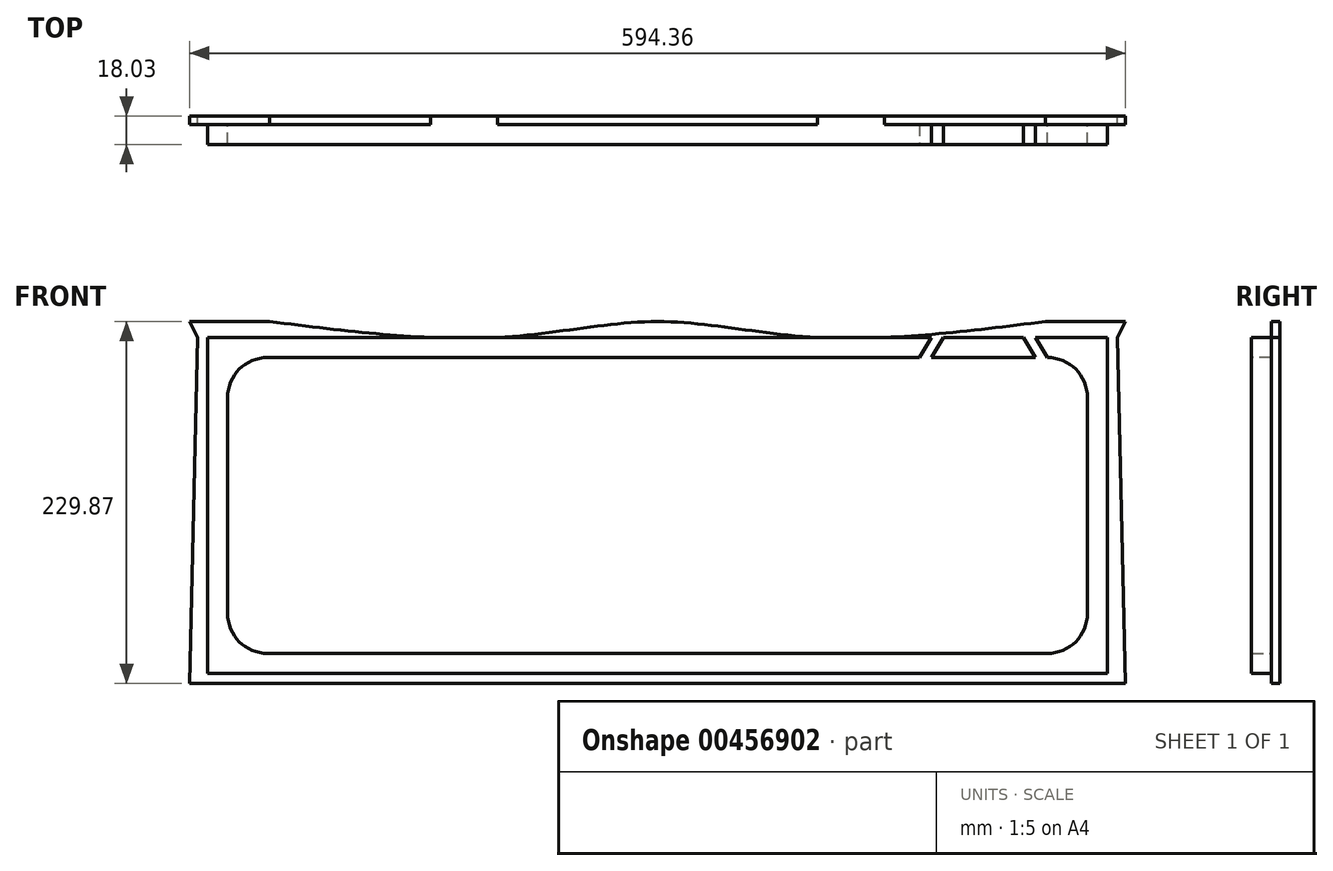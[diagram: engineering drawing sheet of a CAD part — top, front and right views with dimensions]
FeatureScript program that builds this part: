
annotation { "Feature Type Name" : "Feature", "Feature Type Description" : "" }
export const myFeature = defineFeature(function(context is Context, id is Id, definition is map)
    precondition{}
    {
        {
            var Q0;
            Q0=qCreatedBy(makeId("Front.planeOp"),FACE);
            var sketch = newSketch(context, id + "F0", { "sketchPlane" : qUnion([Q0])});
            skLineSegment(sketch, "E0.bottom", {"start": v(0, 0) * mm, "end": v(-584.2, 0) * mm});
            skLineSegment(sketch, "E0.top", {"start": v(0, 219.7) * mm, "end": v(-584.2, 219.7) * mm});
            skLineSegment(sketch, "E0.left", {"start": v(0, 0) * mm, "end": v(0, 219.7) * mm});
            skLineSegment(sketch, "E0.right", {"start": v(-584.2, 0) * mm, "end": v(-584.2, 219.7) * mm});
            skPoint(sketch, "E1", {"position": v(-292.1, 219.7) * mm});
            skSolve(sketch);
        }
        {
            var Q0;
            Q0=makeQuery(id+"F0.imprint","IMPRINT",FACE,{"disambiguationData":[TD([[makeQuery(id+"F0.imprint","IMPRINT",EDGE,{"derivedFrom":sQuery(id+"F0.wireOp",EDGE,"E0.bottom")}),-1.0]])]});
            extrude(context, id + "F1", {"entities" : qUnion([Q0]), "depth" : 5.33 * mm});
        }
        {
            var Q0;
            Q0=makeQuery(id+"F1.opExtrude","CAP_FACE",FACE,{"disambiguationData":[OSD([sQuery(id+"F0.wireOp",EDGE,"E0.bottom"),sQuery(id+"F0.wireOp",EDGE,"E0.top"),sQuery(id+"F0.wireOp",EDGE,"E0.left"),sQuery(id+"F0.wireOp",EDGE,"E0.right")])],"isStart":false});
            var sketch = newSketch(context, id + "F2", { "sketchPlane" : qUnion([Q0])});
            skLineSegment(sketch, "E2", {"start": v(-577.85, 219.7) * mm, "end": v(-577.85, 6.35) * mm});
            skLineSegment(sketch, "E3", {"start": v(-577.85, 6.35) * mm, "end": v(-6.35, 6.35) * mm});
            skLineSegment(sketch, "E4", {"start": v(-6.35, 6.35) * mm, "end": v(-6.35, 219.71) * mm});
            skLineSegment(sketch, "E5", {"start": v(-6.35, 219.71) * mm, "end": v(-577.85, 219.7) * mm});
            skLineSegment(sketch, "E6", {"start": v(-565.15, 207) * mm, "end": v(-565.15, 19.05) * mm});
            skLineSegment(sketch, "E7", {"start": v(-565.15, 19.05) * mm, "end": v(-19.05, 19.05) * mm});
            skLineSegment(sketch, "E8", {"start": v(-19.05, 19.05) * mm, "end": v(-19.05, 207.01) * mm});
            skLineSegment(sketch, "E9", {"start": v(-19.05, 207.01) * mm, "end": v(-565.15, 207) * mm});
            skSolve(sketch);
        }
        {
            var Q0;
            Q0=makeQuery(id+"F2.imprint","IMPRINT",FACE,{"disambiguationData":[TD([[makeQuery(id+"F2.imprint","IMPRINT",EDGE,{"derivedFrom":sQuery(id+"F2.wireOp",EDGE,"E2")}),1.0]])]});
            extrude(context, id + "F3", {"entities" : qUnion([Q0]), "operationType" : NewBodyOperationType.ADD, "depth" : 12.7 * mm});
        }
        {
            var Q0;
            Q0=makeQuery(id+"F3.opExtrude","SWEPT_EDGE",EDGE,{"disambiguationData":[OSD([sQuery(id+"F2.wireOp",EDGE,"E6"),sQuery(id+"F2.wireOp",EDGE,"E9")])]});
            var Q1;
            Q1=makeQuery(id+"F3.opExtrude","SWEPT_EDGE",EDGE,{"disambiguationData":[OSD([sQuery(id+"F2.wireOp",EDGE,"E8"),sQuery(id+"F2.wireOp",EDGE,"E9")])]});
            var Q2;
            Q2=makeQuery(id+"F3.opExtrude","SWEPT_EDGE",EDGE,{"disambiguationData":[OSD([sQuery(id+"F2.wireOp",EDGE,"E7"),sQuery(id+"F2.wireOp",EDGE,"E8")])]});
            var Q3;
            Q3=makeQuery(id+"F3.opExtrude","SWEPT_EDGE",EDGE,{"disambiguationData":[OSD([sQuery(id+"F2.wireOp",EDGE,"E6"),sQuery(id+"F2.wireOp",EDGE,"E7")])]});
            fillet(context, id + "F4", {"entities" : qUnion([Q0, Q1, Q2, Q3]), "radius" : 25.4 * mm, "tangentPropagation" : true, "allowEdgeOverflow" : false});
        }
        {
            var Q0;
            Q0=makeQuery(id+"F3.opExtrude","CAP_FACE",FACE,{"disambiguationData":[OSD([sQuery(id+"F2.wireOp",EDGE,"E2"),sQuery(id+"F2.wireOp",EDGE,"E3"),sQuery(id+"F2.wireOp",EDGE,"E4"),sQuery(id+"F2.wireOp",EDGE,"E5"),sQuery(id+"F2.wireOp",EDGE,"E6"),sQuery(id+"F2.wireOp",EDGE,"E7"),sQuery(id+"F2.wireOp",EDGE,"E8"),sQuery(id+"F2.wireOp",EDGE,"E9")])],"isStart":false});
            var sketch = newSketch(context, id + "F5", { "sketchPlane" : qUnion([Q0])});
            skPoint(sketch, "E10", {"position": v(-118.11, 219.7) * mm});
            skPoint(sketch, "E11", {"position": v(-110.5, 219.7) * mm});
            skPoint(sketch, "E12", {"position": v(-59.69, 219.7) * mm});
            skPoint(sketch, "E13", {"position": v(-52.07, 219.7) * mm});
            skPoint(sketch, "E14", {"position": v(-376.28, 272.75) * mm});
            skPoint(sketch, "E15", {"position": v(-12.7, 0) * mm});
            skPoint(sketch, "E16", {"position": v(-20.32, 0) * mm});
            skLineSegment(sketch, "E17", {"start": v(-20.32, 0) * mm, "end": v(-12.7, 0) * mm});
            skPoint(sketch, "E18", {"position": v(-118.11, 207.01) * mm});
            skPoint(sketch, "E19", {"position": v(-125.73, 207.01) * mm});
            skLineSegment(sketch, "E20", {"start": v(-125.73, 207.01) * mm, "end": v(-118.11, 219.7) * mm});
            skLineSegment(sketch, "E21", {"start": v(-125.73, 207.01) * mm, "end": v(-118.11, 207.01) * mm});
            skLineSegment(sketch, "E22", {"start": v(-118.11, 207.01) * mm, "end": v(-110.5, 219.7) * mm});
            skLineSegment(sketch, "E23", {"start": v(-118.11, 219.7) * mm, "end": v(-110.5, 219.7) * mm});
            skLineSegment(sketch, "E24", {"start": v(-59.69, 219.7) * mm, "end": v(-52.07, 219.7) * mm});
            skLineSegment(sketch, "E25", {"start": v(-110.5, 219.7) * mm, "end": v(-59.69, 219.7) * mm});
            skLineSegment(sketch, "E26", {"start": v(-59.69, 219.7) * mm, "end": v(-110.5, 219.7) * mm});
            skLineSegment(sketch, "E27", {"start": v(-110.5, 219.7) * mm, "end": v(-113.58, 214.56) * mm});
            skPoint(sketch, "E28", {"position": v(-44.45, 207.01) * mm});
            skPoint(sketch, "E29", {"position": v(-52.07, 207.01) * mm});
            skLineSegment(sketch, "E30", {"start": v(-59.69, 219.7) * mm, "end": v(-52.07, 207.01) * mm});
            skLineSegment(sketch, "E31", {"start": v(-52.07, 219.7) * mm, "end": v(-44.45, 207.01) * mm});
            skLineSegment(sketch, "E32", {"start": v(-52.07, 207.01) * mm, "end": v(-44.45, 207.01) * mm});
            skLineSegment(sketch, "E33", {"start": v(-52.07, 219.7) * mm, "end": v(-59.69, 219.7) * mm});
            skPoint(sketch, "E34", {"position": v(-56.6, 214.56) * mm});
            skLineSegment(sketch, "E35", {"start": v(-113.58, 214.56) * mm, "end": v(-56.6, 214.56) * mm});
            skSolve(sketch);
        }
        {
            var Q0;
            Q0=makeQuery(id+"F5.imprint","IMPRINT",FACE,{"disambiguationData":[TD([[makeQuery(id+"F5.imprint","IMPRINT",EDGE,{"derivedFrom":sQuery(id+"F5.wireOp",EDGE,"E20")}),-1.0]])]});
            var Q1;
            {var subQ8=sQuery(id+"F5.wireOp",EDGE,"RZINdJYM-ykuw-GilU-JIjt-DnibDYUsXZuo");Q1=makeQuery(id+"F5.imprint","IMPRINT",FACE,{"disambiguationData":[TD([[makeQuery(id+"F5.imprint","IMPRINT",EDGE,{"derivedFrom":subQ8}),1.0]])]});}
            var Q2;
            Q2=makeQuery(id+"F5.imprint","IMPRINT",FACE,{"disambiguationData":[TD([[makeQuery(id+"F5.imprint","IMPRINT",EDGE,{"derivedFrom":sQuery(id+"F5.wireOp",EDGE,"RZINdJYM-ykuw-GilU-JIjt-DnibDYUsXZuo")}),-1.0]])]});
            var Q3;
            Q3=makeQuery(id+"F5.imprint","IMPRINT",FACE,{"disambiguationData":[TD([[makeQuery(id+"F5.imprint","IMPRINT",EDGE,{"derivedFrom":sQuery(id+"F5.wireOp",EDGE,"NQJIxGkc-Vixr-o2zM-VUe3-bVQ5EoZFKsab")}),1.0]])]});
            var Q4;
            Q4=makeQuery(id+"F5.imprint","IMPRINT",FACE,{"disambiguationData":[TD([[makeQuery(id+"F5.imprint","IMPRINT",EDGE,{"derivedFrom":sQuery(id+"F5.wireOp",EDGE,"E30")}),1.0]])]});
            var Q5;
            {var subQ0=sQuery(id+"F5.wireOp",EDGE,"E26");Q5=makeQuery(id+"F5.imprint","IMPRINT",FACE,{"disambiguationData":[TD([[makeQuery(id+"F5.imprint","IMPRINT",EDGE,{"derivedFrom":subQ0}),1.0]])]});}
            extrude(context, id + "F6", {"entities" : qUnion([Q0, Q1, Q2, Q3, Q4, Q5]), "operationType" : NewBodyOperationType.REMOVE, "oppositeDirection" : true, "depth" : 12.7 * mm});
        }
        {
            var Q0;
            Q0=makeQuery(id+"F1.opExtrude","CAP_FACE",FACE,{"disambiguationData":[OSD([sQuery(id+"F0.wireOp",EDGE,"E0.bottom"),sQuery(id+"F0.wireOp",EDGE,"E0.top"),sQuery(id+"F0.wireOp",EDGE,"E0.left"),sQuery(id+"F0.wireOp",EDGE,"E0.right")])],"isStart":true});
            var sketch = newSketch(context, id + "F7", { "sketchPlane" : qUnion([Q0])});
            skLineSegment(sketch, "E36", {"start": v(0, 0) * mm, "end": v(-5.08, 0) * mm});
            skLineSegment(sketch, "E37", {"start": v(-5.08, 0) * mm, "end": v(-5.08, 229.87) * mm});
            skLineSegment(sketch, "E38", {"start": v(-5.08, 229.87) * mm, "end": v(589.28, 229.87) * mm});
            skLineSegment(sketch, "E39", {"start": v(589.28, 229.87) * mm, "end": v(589.28, 0) * mm});
            skLineSegment(sketch, "E40", {"start": v(589.28, 0) * mm, "end": v(584.2, 0) * mm});
            skPoint(sketch, "E41", {"position": v(589.28, 114.93) * mm});
            skPoint(sketch, "E42", {"position": v(584.2, 109.85) * mm});
            skPoint(sketch, "E43", {"position": v(292.1, 229.87) * mm});
            skPoint(sketch, "E44", {"position": v(292.1, 219.7) * mm});
            skPoint(sketch, "E45", {"position": v(-5.08, 114.93) * mm});
            skPoint(sketch, "E46", {"position": v(0, 109.85) * mm});
            skPoint(sketch, "E47", {"position": v(538.48, 229.87) * mm});
            skPoint(sketch, "E48", {"position": v(45.72, 229.87) * mm});
            skPoint(sketch, "E49", {"position": v(-5.08, 191.77) * mm});
            skPoint(sketch, "E50", {"position": v(589.28, 191.77) * mm});
            skPoint(sketch, "E51", {"position": v(584.2, 183.25) * mm});
            skPoint(sketch, "E52", {"position": v(0, 176.13) * mm});
            skPoint(sketch, "E53", {"position": v(589.28, 63.5) * mm});
            skPoint(sketch, "E54", {"position": v(-5.08, 63.5) * mm});
            skPoint(sketch, "E55", {"position": v(0, 219.7) * mm});
            skPoint(sketch, "E56", {"position": v(584.2, 219.7) * mm});
            skPoint(sketch, "E57", {"position": v(393.7, 219.7) * mm});
            skPoint(sketch, "E58", {"position": v(190.5, 219.7) * mm});
            skFitSpline(sketch, "E59", {"points": [v(538.48, 229.87) * mm, v(393.7, 219.7) * mm, v(292.1, 229.87) * mm, v(190.5, 219.7) * mm, v(45.72, 229.87) * mm], "startDerivative": vector(-556.08, -69.34) * mm, "endDerivative": vector(-556.08, 69.34) * mm});
            skLineSegment(sketch, "E60", {"start": v(589.28, 229.87) * mm, "end": v(584.2, 219.7) * mm});
            skLineSegment(sketch, "E61", {"start": v(584.2, 219.7) * mm, "end": v(589.28, 0) * mm});
            skLineSegment(sketch, "E62", {"start": v(-5.08, 229.87) * mm, "end": v(0, 219.7) * mm});
            skLineSegment(sketch, "E63", {"start": v(0, 219.7) * mm, "end": v(-5.08, 0) * mm});
            skSolve(sketch);
        }
        {
            var Q0;
            Q0=makeQuery(id+"F7.imprint","IMPRINT",FACE,{"disambiguationData":[TD([[makeQuery(id+"F7.imprint","IMPRINT",EDGE,{"derivedFrom":sQuery(id+"F7.wireOp",EDGE,"E40")}),-1.0]])]});
            var Q1;
            {var subQ0=sQuery(id+"F7.wireOp",EDGE,"E60");Q1=makeQuery(id+"F7.imprint","IMPRINT",FACE,{"disambiguationData":[TD([[makeQuery(id+"F7.imprint","IMPRINT",EDGE,{"derivedFrom":subQ0}),-1.0]])]});}
            var Q2;
            {var subQ0=sQuery(id+"F7.wireOp",EDGE,"E59");var subQ1=makeQuery(id+"F7.imprint","INTERSECT",VERTEX,{"disambiguationData":[OD(2.0)],"derivedFrom":[sQuery(id+"F7.wireOp",EDGE,"E38"),subQ0]});Q2=makeQuery(id+"F7.imprint","IMPRINT",FACE,{"disambiguationData":[TD([[makeQuery(id+"F7.imprint","IMPRINT",EDGE,{"disambiguationData":[TD([[subQ1,1.0]])],"derivedFrom":subQ0}),1.0]])]});}
            var Q3;
            {var subQ0=sQuery(id+"F7.wireOp",EDGE,"E62");Q3=makeQuery(id+"F7.imprint","IMPRINT",FACE,{"disambiguationData":[TD([[makeQuery(id+"F7.imprint","IMPRINT",EDGE,{"derivedFrom":subQ0}),1.0]])]});}
            var Q4;
            Q4=makeQuery(id+"F7.imprint","IMPRINT",FACE,{"disambiguationData":[TD([[makeQuery(id+"F7.imprint","IMPRINT",EDGE,{"derivedFrom":sQuery(id+"F7.wireOp",EDGE,"E36")}),-1.0]])]});
            extrude(context, id + "F8", {"entities" : qUnion([Q0, Q1, Q2, Q3, Q4]), "operationType" : NewBodyOperationType.ADD, "depth" : -5.33 * mm});
        }
    });
